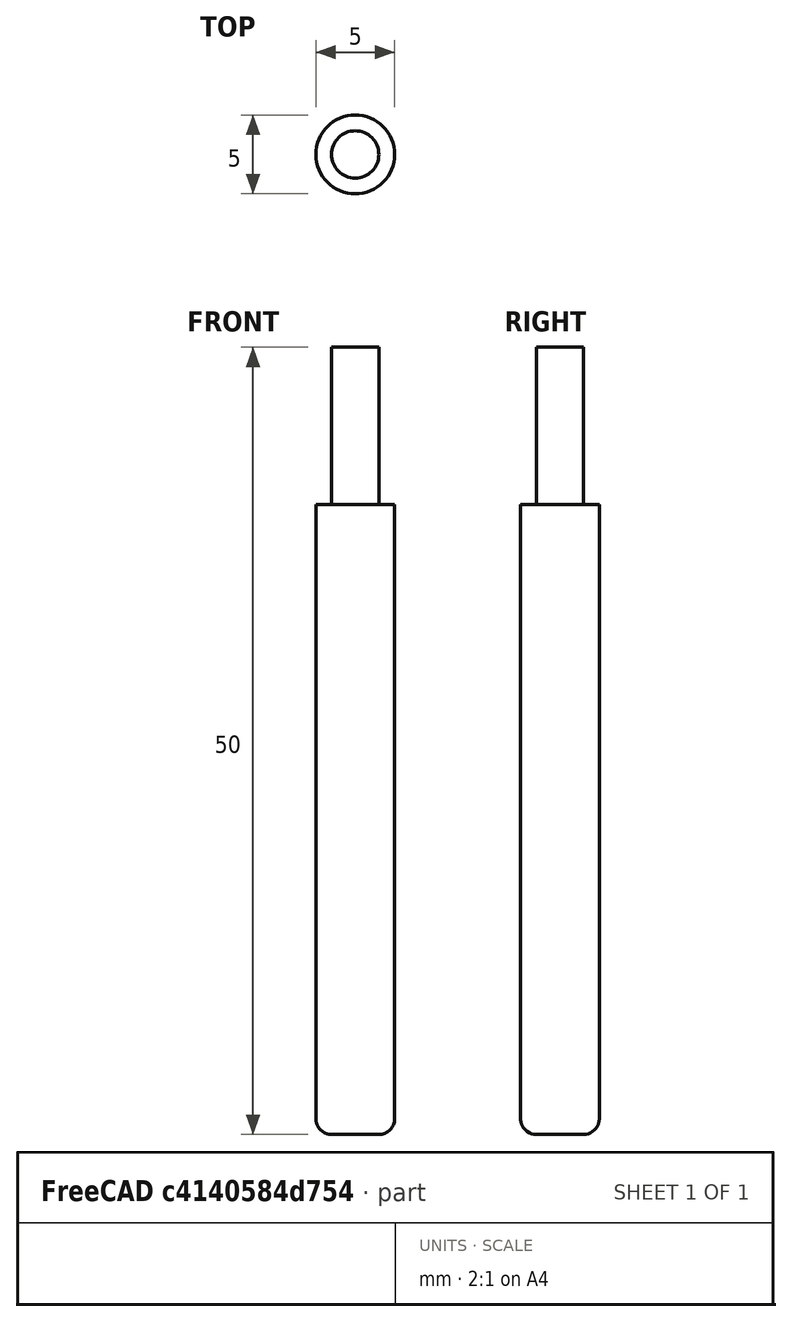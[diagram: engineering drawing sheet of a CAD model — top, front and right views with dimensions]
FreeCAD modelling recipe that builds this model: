
FCSTD DOCUMENT  (FreeCAD 0.19R20874 (Git))
Label: bullnose
License: All rights reserved
LicenseURL: http://en.wikipedia.org/wiki/All_rights_reserved
objects: Sketcher::SketchObject×1, PartDesign::Revolution×1, PartDesign::Body×1
note: 4 computed .brp shape members not serialized (recipe doc carries the construction recipe); baked Part::Feature solids carry a one-line shape summary decoded from their .brp

FEATURE [Sketcher::SketchObject] Sketch
  MapMode = 5
  Placement = pos=(0,0,0) rot=(1,0,0;1.5708rad)
  Support = -> [XZ_Plane]
  sketch-geometry (9):
    g0: LineSegment StartX=0 StartY=50 StartZ=0 EndX=0 EndY=0 EndZ=0
    g1: LineSegment StartX=0 StartY=0 StartZ=0 EndX=1.5 EndY=0 EndZ=0
    g2: LineSegment StartX=2.5 StartY=1 StartZ=0 EndX=2.5 EndY=40 EndZ=0
    g3: LineSegment StartX=1.5 StartY=50 StartZ=0 EndX=0 EndY=50 EndZ=0
    g4: LineSegment [constr] StartX=2.5 StartY=0 StartZ=0 EndX=-2.5 EndY=0 EndZ=0
    g5: LineSegment StartX=1.5 StartY=40 StartZ=0 EndX=2.5 EndY=40 EndZ=0
    g6: LineSegment StartX=1.5 StartY=50 StartZ=0 EndX=1.5 EndY=40 EndZ=0
    g7: LineSegment [constr] StartX=-1.5 StartY=50 StartZ=0 EndX=1.5 EndY=50 EndZ=0
    g8: ArcOfCircle CenterX=1.5 CenterY=1 CenterZ=0 NormalX=0 NormalY=0 NormalZ=1 AngleXU=0 Radius=1 StartAngle=4.71239 EndAngle=6.28319
  constraints (24):
    c: Vertical(g0)
    c: Coincident(g0,g1)
    c: Horizontal(g1)
    c: Vertical(g2)
    c: Horizontal(g3)
    c: DistanceX(g4,g4) = 5  'Diameter; Endmill diameter'
    c: DistanceY(g4,g3) = 50  'Length; Overall length of the endmill'
    c: Horizontal(g5)
    c: Coincident(g2,g5)
    c: Vertical(g6)
    c: Coincident(g3,g6)
    c: Symmetric(g7,g7,g0)
    c: Coincident(g7,g3)
    c: DistanceX(g7,g7) = 3  'ShankDiameter; diameter of the shank'
    c: Coincident(g5,g6)
    c: Tangent(g1,g8) = -1.5708
    c: Tangent(g2,g8) = -1.5708
    c: PointOnObject(g0,g4)
    c: Symmetric(g4,g4,g-2)
    c: Vertical(g4,g2)
    c: DistanceX(g1,g1) = 1.5  'FlatRadius;Radius of the bottom flat part.'
    c: DistanceY(g1,g2) = 40  'CuttingEdgeHeight'
    c: Coincident(g0,g3)
    c: Coincident(g-1,g0)
FEATURE [PartDesign::Revolution] Revolution
  AllowMultiFace = false
  Angle = 360
  Axis = (0,-2e-16,1)
  Base = (0,0,0)
  Placement = pos=(0,0,0) rot=(1,0,0;1.5708rad)
  Profile = -> Sketch
  ReferenceAxis = -> Sketch [V_Axis]
  Reversed = true
FEATURE [PartDesign::Body] Body  label="Bullnose"
  Group = -> [Sketch,Revolution]
  Origin = -> Origin
  Tip = -> Revolution
